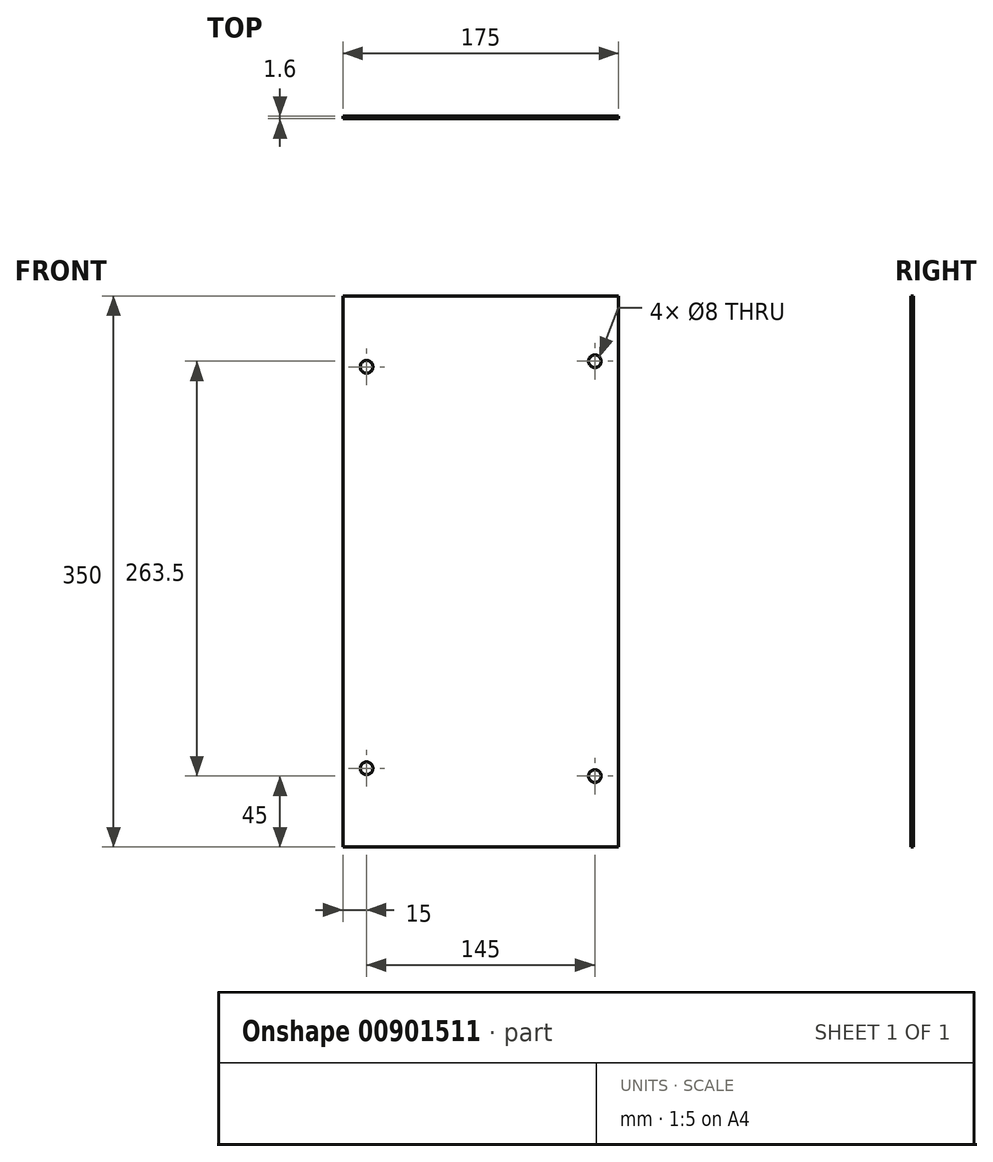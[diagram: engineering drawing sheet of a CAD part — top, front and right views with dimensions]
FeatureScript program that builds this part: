
annotation { "Feature Type Name" : "Feature", "Feature Type Description" : "" }
export const myFeature = defineFeature(function(context is Context, id is Id, definition is map)
    precondition{}
    {
        {
            var Q0;
            Q0=qCreatedBy(makeId("Front.planeOp"),FACE);
            var sketch = newSketch(context, id + "F0", { "sketchPlane" : qUnion([Q0])});
            skLineSegment(sketch, "E0.bottom", {"start": v(0, 0) * mm, "end": v(175, 0) * mm});
            skLineSegment(sketch, "E0.top", {"start": v(0, -350) * mm, "end": v(175, -350) * mm});
            skLineSegment(sketch, "E0.left", {"start": v(0, 0) * mm, "end": v(0, -350) * mm});
            skLineSegment(sketch, "E0.right", {"start": v(175, 0) * mm, "end": v(175, -350) * mm});
            skPoint(sketch, "E1", {"position": v(15, -45) * mm});
            skPoint(sketch, "E2", {"position": v(15, -300) * mm});
            skPoint(sketch, "E3", {"position": v(160, -41.5) * mm});
            skPoint(sketch, "E4", {"position": v(160, -305) * mm});
            skSolve(sketch);
        }
        {
            var Q0;
            Q0 = qSketchRegion(id + "F0", true);
            extrude(context, id + "F1", {"entities" : qUnion([Q0]), "depth" : 1.6 * mm, "offsetDistance" : 25 * mm});
        }
        {
            var Q0;
            Q0=sQuery(id+"F0.wireOp",VERTEX,"E1");
            var Q1;
            Q1=sQuery(id+"F0.wireOp",VERTEX,"E3");
            var Q2;
            Q2=sQuery(id+"F0.wireOp",VERTEX,"E4");
            var Q3;
            Q3=sQuery(id+"F0.wireOp",VERTEX,"E2");
            var Q4;
            Q4=makeQuery(id+"F1.opExtrude","SWEPT_BODY",BODY,{"disambiguationData":[OSD([sQuery(id+"F0.wireOp",EDGE,"E0.bottom"),sQuery(id+"F0.wireOp",EDGE,"E0.top"),sQuery(id+"F0.wireOp",EDGE,"E0.left"),sQuery(id+"F0.wireOp",EDGE,"E0.right")])]});
            hole(context, id + "F2", {"style" : HoleStyle.SIMPLE, "endStyle" : HoleEndStyle.THROUGH, "oppositeDirection" : true, "standardTappedOrClearance" : lookupTablePath({ "standard" : "ISO", "size" : "8", "type" : "Drilled" }), "standardBlindInLast" : lookupTablePath({ "standard" : "ISO", "size" : "8", "type" : "Drilled" }), "holeDiameter" : 8 * mm, "majorDiameter" : 5 * mm, "isTappedThrough" : true, "tappedDepth" : 11.5 * mm, "tapClearance" : 3, "startFromSketch" : true, "locations" : qUnion([Q0, Q1, Q2, Q3]), "scope" : qUnion([Q4])});
        }
    });
